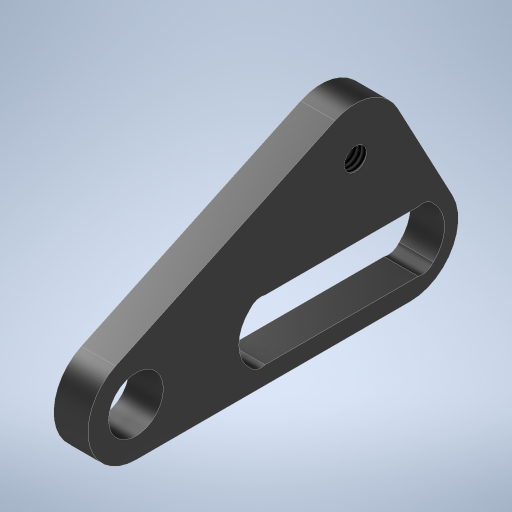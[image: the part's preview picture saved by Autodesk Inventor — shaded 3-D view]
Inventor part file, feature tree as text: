
AUTODESK INVENTOR PART (.ipt)
format: ipt  version: 2024.2 (Build 282272000, 272)  size: 287,232 bytes
history: native  units: mm
features: sketch x1, extrude x1, hole x1
ambient origin geometry x8: Origin, YZ Plane, XZ Plane, XY Plane, X Axis, Y Axis, Z Axis, Center Point
bodies: Solid1 (feature_tree)
feature tree (3):
  sketch  "Sketch1"  dims[d0=32.0mm d1=15.0mm d2=20.0mm d3=60.0deg d4=20.0mm d5=10.0mm d6=8.8mm d7=20.0mm d9=14.0mm d10=2.0mm d11=5.0mm d12=0.0mm d13=8.0mm d14=6.0mm d15=4.0mm d16=2.0mm d17=90.0deg d18=8.0mm d19=20.594885mm d20=8.0mm d22=8.1mm d23=3.242mm d24=8.0mm d25=4.0mm d26=2.0mm d27=90.0deg d28=8.0mm d29=20.594885mm]
  extrude  "Extrusion1"  Depth=2.0mm
  hole  "Phi8.0-h7"  [1 undecoded]
note: 1 required parameter value undecoded (feature->parameter linkage not recoverable at this tier; creation-order binding heuristic only, values carry confidence <= 0.55)
